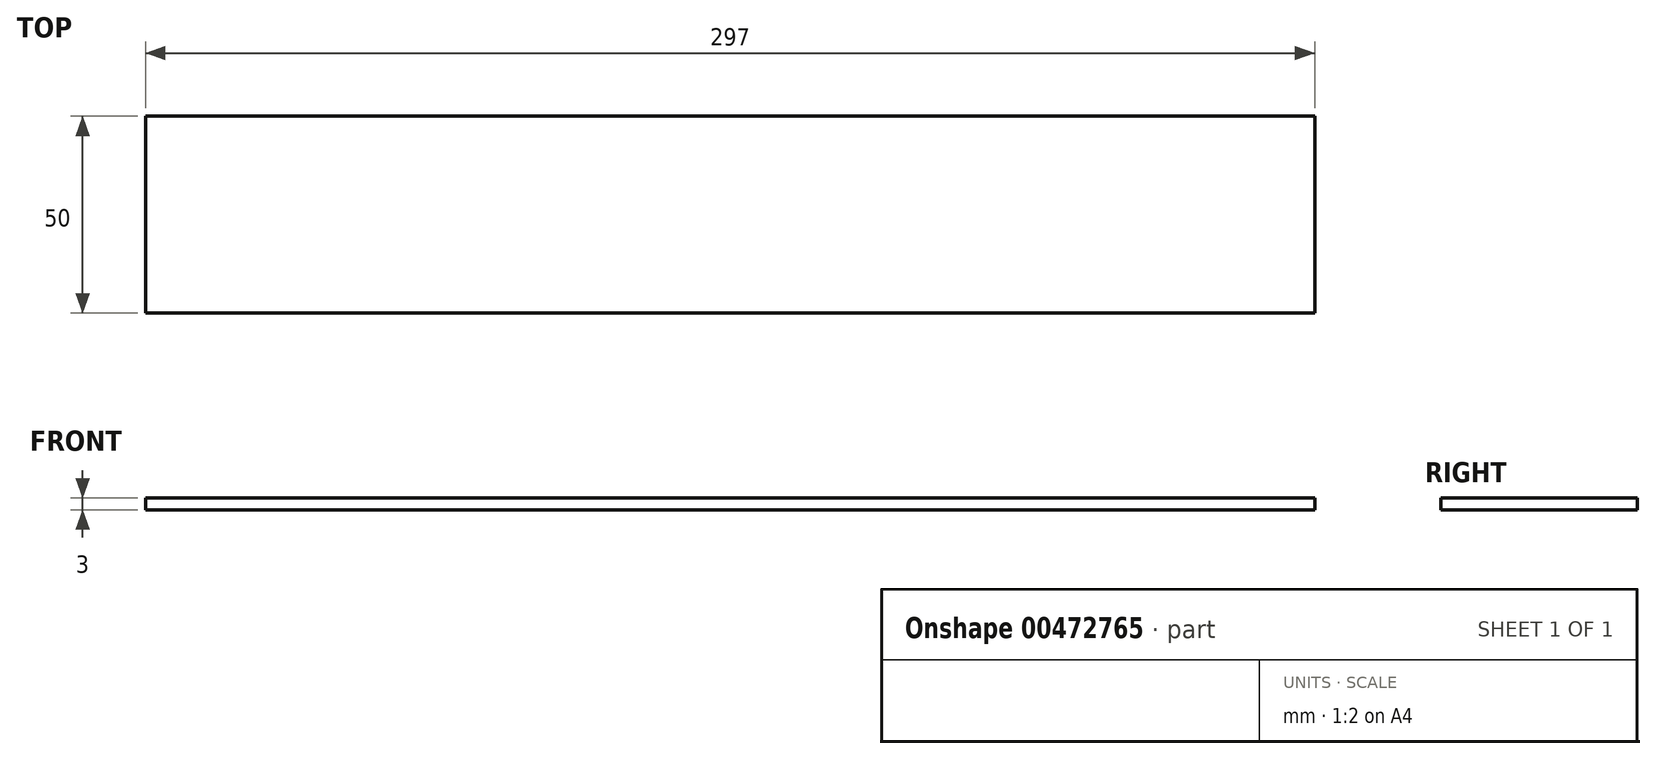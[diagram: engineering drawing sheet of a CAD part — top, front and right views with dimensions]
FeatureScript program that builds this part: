
annotation { "Feature Type Name" : "Feature", "Feature Type Description" : "" }
export const myFeature = defineFeature(function(context is Context, id is Id, definition is map)
    precondition{}
    {
        {
            assignVariable(context, id + "F0", {"name" : "e", "anyValue" : 3});
        }
        {
            var Q0;
            Q0=qCreatedBy(makeId("Top.planeOp"),FACE);
            var sketch = newSketch(context, id + "F1", { "sketchPlane" : qUnion([Q0])});
            skLineSegment(sketch, "E0.bottom", {"start": v(0, 0) * mm, "end": v(297, 0) * mm});
            skLineSegment(sketch, "E0.top", {"start": v(0, 50) * mm, "end": v(297, 50) * mm});
            skLineSegment(sketch, "E0.left", {"start": v(0, 0) * mm, "end": v(0, 50) * mm});
            skLineSegment(sketch, "E0.right", {"start": v(297, 0) * mm, "end": v(297, 50) * mm});
            skSolve(sketch);
        }
        {
            var Q0;
            Q0 = qSketchRegion(id + "F1", true);
            extrude(context, id + "F2", {"entities" : qUnion([Q0]), "offsetDistance" : 25 * mm, "depth" : (getVariable(context, 'e')) * mm});
        }
    });
